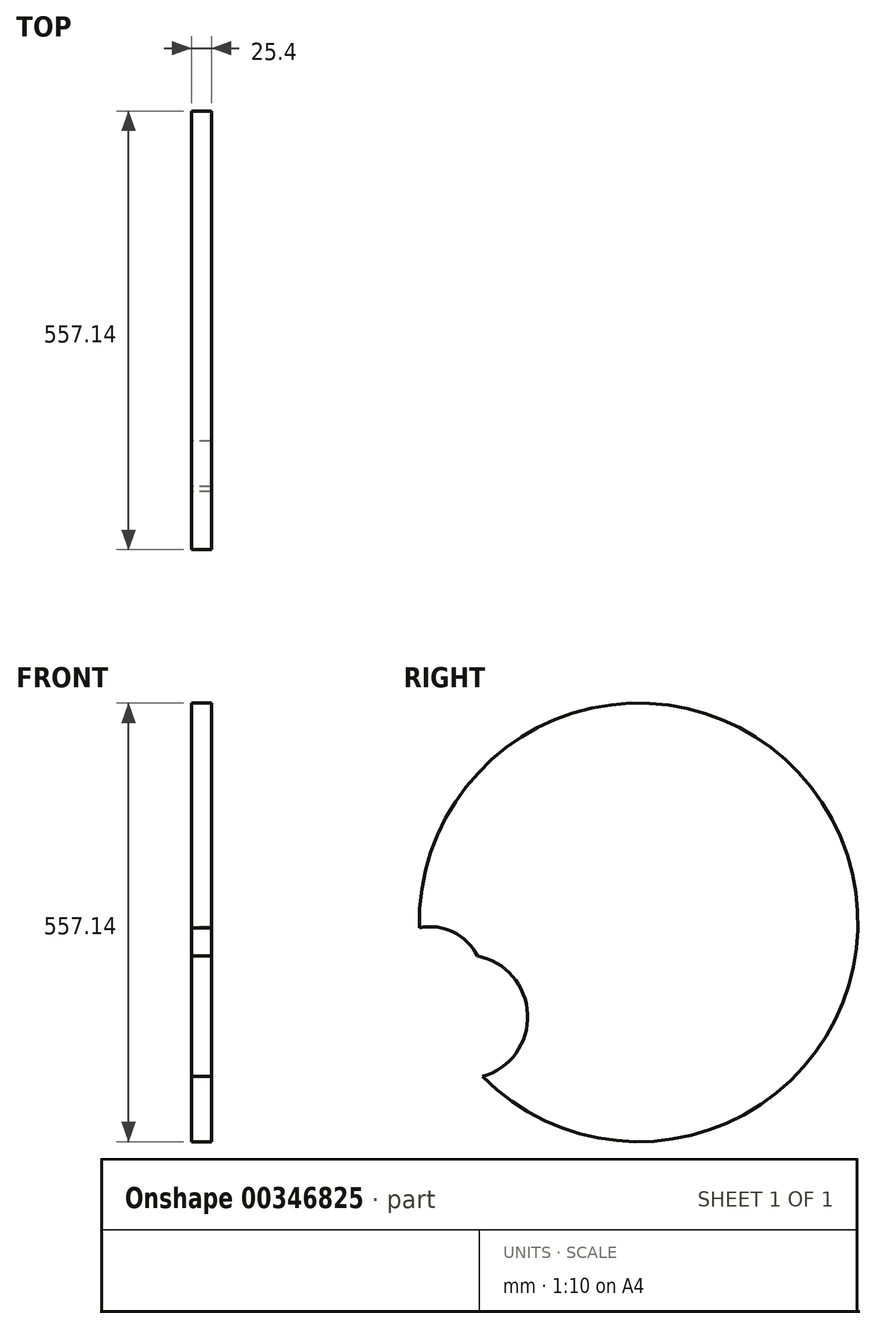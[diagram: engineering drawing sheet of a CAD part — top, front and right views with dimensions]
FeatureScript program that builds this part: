
annotation { "Feature Type Name" : "Feature", "Feature Type Description" : "" }
export const myFeature = defineFeature(function(context is Context, id is Id, definition is map)
    precondition{}
    {
        {
            var Q0;
            Q0=qCreatedBy(makeId("Right.planeOp"),FACE);
            var sketch = newSketch(context, id + "F0", { "sketchPlane" : qUnion([Q0])});
            skCircle(sketch, "E0", {"center": v(-57.85, 33.39) * mm, "radius": 66.8 * mm});
            skPoint(sketch, "E0.first.point", {"position": v(0, 0) * mm});
            skPoint(sketch, "E0.second.point", {"position": v(0, 66.78) * mm});
            skPoint(sketch, "E0.third.point", {"position": v(-92.33, -23.82) * mm});
            skCircle(sketch, "E1", {"center": v(206.8, 105.66) * mm, "radius": 278.57 * mm});
            skPoint(sketch, "E1.first.point", {"position": v(-69.67, 71.4) * mm});
            skPoint(sketch, "E1.second.point", {"position": v(-43.83, -15.96) * mm});
            skPoint(sketch, "E1.third.point", {"position": v(-60.2, 26.16) * mm});
            skCircle(sketch, "E2", {"center": v(-12.76, -14.34) * mm, "radius": 78.7 * mm});
            skPoint(sketch, "E2.first.point", {"position": v(-90.83, -4.29) * mm});
            skPoint(sketch, "E2.second.point", {"position": v(65.87, -17.68) * mm});
            skPoint(sketch, "E2.third.point", {"position": v(-72.33, 37.1) * mm});
            skSolve(sketch);
        }
        {
            var Q0;
            {var subQ0=sQuery(id+"F0.wireOp",EDGE,"E1");var subQ1=sQuery(id+"F0.wireOp",EDGE,"E0");var subQ2=makeQuery(id+"F0.imprint","INTERSECT",VERTEX,{"disambiguationData":[OD(0.0)],"derivedFrom":[subQ1,subQ0]});Q0=makeQuery(id+"F0.imprint","IMPRINT",FACE,{"disambiguationData":[TD([[makeQuery(id+"F0.imprint","IMPRINT",EDGE,{"disambiguationData":[TD([[subQ2,1.0]])],"derivedFrom":subQ1}),-1.0]])]});}
            extrude(context, id + "F1", {"entities" : qUnion([Q0]), "depth" : 25.4 * mm});
        }
    });
